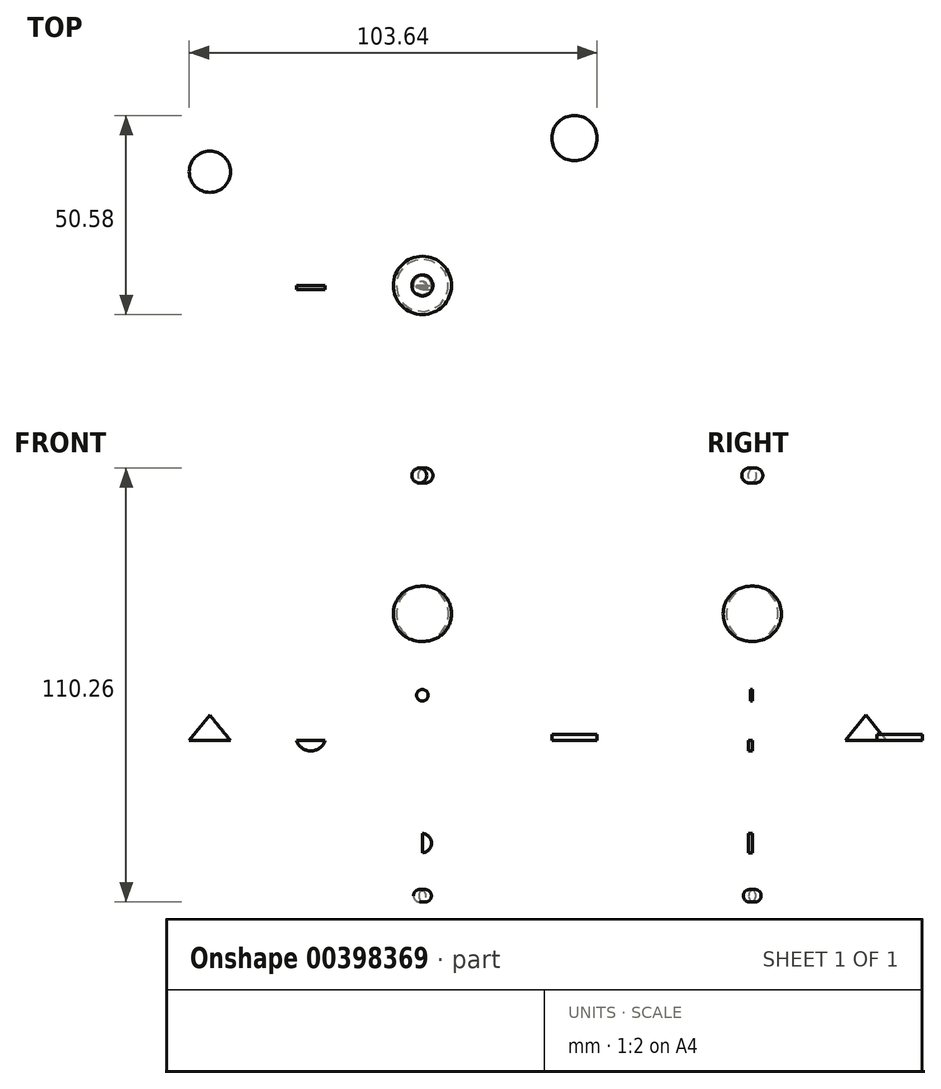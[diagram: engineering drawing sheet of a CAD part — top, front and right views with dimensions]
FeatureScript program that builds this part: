
annotation { "Feature Type Name" : "Feature", "Feature Type Description" : "" }
export const myFeature = defineFeature(function(context is Context, id is Id, definition is map)
    precondition{}
    {
        {
            var Q0;
            Q0=qCreatedBy(makeId("Front.planeOp"),FACE);
            var sketch = newSketch(context, id + "F0", { "sketchPlane" : qUnion([Q0])});
            skLineSegment(sketch, "E0", {"start": v(0, 39.22) * mm, "end": v(0, 25.22) * mm});
            skArc(sketch, "E1", {"start": v(0, 25.22) * mm, "mid": v(6.61, 32.22) * mm, "end": v(0, 39.22) * mm});
            skSolve(sketch);
        }
        {
            var Q0;
            Q0=makeQuery(id+"F0.imprint","IMPRINT",FACE,{"disambiguationData":[TD([[makeQuery(id+"F0.imprint","IMPRINT",EDGE,{"derivedFrom":sQuery(id+"F0.wireOp",EDGE,"E0")}),1.0]])]});
            var Q1;
            Q1=sQuery(id+"F0.wireOp",EDGE,"E0");
            revolve(context, id + "F1", {"entities" : qUnion([Q0]), "axis" : qUnion([Q1]), "revolveType" : RevolveType.FULL});
        }
        {
            var Q0;
            Q0=qCreatedBy(makeId("Top.planeOp"),FACE);
            var sketch = newSketch(context, id + "F2", { "sketchPlane" : qUnion([Q0])});
            skCircle(sketch, "E2", {"center": v(38.65, 37.42) * mm, "radius": 5.76 * mm});
            skPoint(sketch, "E2.first.point", {"position": v(40.8, 42.76) * mm});
            skPoint(sketch, "E2.second.point", {"position": v(33.3, 35.28) * mm});
            skPoint(sketch, "E2.third.point", {"position": v(34.88, 41.78) * mm});
            skSolve(sketch);
        }
        {
            var Q0;
            Q0=makeQuery(id+"F2.imprint","IMPRINT",FACE,{"disambiguationData":[TD([[makeQuery(id+"F2.imprint","IMPRINT",EDGE,{"derivedFrom":sQuery(id+"F2.wireOp",EDGE,"E2")}),1.0]])]});
            extrude(context, id + "F3", {"entities" : qUnion([Q0]), "depth" : 1.52 * mm});
        }
        {
            var Q0;
            Q0=qCreatedBy(makeId("Top.planeOp"),FACE);
            var sketch = newSketch(context, id + "F4", { "sketchPlane" : qUnion([Q0])});
            skCircle(sketch, "E3", {"center": v(-54, 28.87) * mm, "radius": 5.23 * mm});
            skPoint(sketch, "E3.first.point", {"position": v(-57.94, 25.42) * mm});
            skPoint(sketch, "E3.second.point", {"position": v(-50.45, 32.71) * mm});
            skPoint(sketch, "E3.third.point", {"position": v(-50.45, 25.03) * mm});
            skSolve(sketch);
        }
        {
            var Q0;
            Q0=makeQuery(id+"F4.imprint","IMPRINT",FACE,{"disambiguationData":[TD([[makeQuery(id+"F4.imprint","IMPRINT",EDGE,{"derivedFrom":sQuery(id+"F4.wireOp",EDGE,"E3")}),1.0]])]});
            extrude(context, id + "F5", {"entities" : qUnion([Q0]), "depth" : 7.62 * mm, "hasDraft" : true, "draftAngle" : 39 * degree, "draftPullDirection" : true});
        }
        {
            var Q0;
            Q0=qCreatedBy(makeId("Front.planeOp"),FACE);
            var sketch = newSketch(context, id + "F6", { "sketchPlane" : qUnion([Q0])});
            skLineSegment(sketch, "E4", {"start": v(0, -14.97) * mm, "end": v(0, -11.22) * mm});
            skArc(sketch, "E5", {"start": v(0, -14.97) * mm, "mid": v(2.44, -13.1) * mm, "end": v(0, -11.22) * mm});
            skSolve(sketch);
        }
        {
            var Q0;
            Q0=makeQuery(id+"F6.imprint","IMPRINT",FACE,{"disambiguationData":[TD([[makeQuery(id+"F6.imprint","IMPRINT",EDGE,{"derivedFrom":sQuery(id+"F6.wireOp",EDGE,"E4")}),-1.0]])]});
            var Q1;
            Q1=sQuery(id+"F6.wireOp",EDGE,"E4");
            revolve(context, id + "F7", {"entities" : qUnion([Q0]), "axis" : qUnion([Q1]), "revolveType" : RevolveType.FULL});
        }
        {
            var Q0;
            Q0=makeQuery(id+"F7.opRevolve","SWEPT_BODY",BODY,{"disambiguationData":[OSD([sQuery(id+"F6.wireOp",EDGE,"E4"),sQuery(id+"F6.wireOp",EDGE,"E5")])]});
            deleteBodies(context, id + "F8", {"entities" : qUnion([Q0])});
        }
        {
            var Q0;
            Q0=qCreatedBy(makeId("Front.planeOp"),FACE);
            var sketch = newSketch(context, id + "F9", { "sketchPlane" : qUnion([Q0])});
            skLineSegment(sketch, "E6", {"start": v(0, -40.87) * mm, "end": v(0, -38) * mm});
            skArc(sketch, "E7", {"start": v(0, -40.87) * mm, "mid": v(2.27, -39.43) * mm, "end": v(0, -38) * mm});
            skSolve(sketch);
        }
        {
            var Q0;
            Q0=makeQuery(id+"F9.imprint","IMPRINT",FACE,{"disambiguationData":[TD([[makeQuery(id+"F9.imprint","IMPRINT",EDGE,{"derivedFrom":sQuery(id+"F9.wireOp",EDGE,"E6")}),-1.0]])]});
            var Q1;
            Q1=sQuery(id+"F9.wireOp",EDGE,"E6");
            revolve(context, id + "F10", {"entities" : qUnion([Q0]), "axis" : qUnion([Q1]), "revolveType" : RevolveType.FULL});
        }
        {
            var Q0;
            Q0=qCreatedBy(makeId("Front.planeOp"),FACE);
            var sketch = newSketch(context, id + "F11", { "sketchPlane" : qUnion([Q0])});
            skLineSegment(sketch, "E8", {"start": v(0, -28.5) * mm, "end": v(0, -23.6) * mm});
            skArc(sketch, "E9", {"start": v(0, -28.5) * mm, "mid": v(2.3, -26.05) * mm, "end": v(0, -23.6) * mm});
            skSolve(sketch);
        }
        {
            var Q0;
            Q0=makeQuery(id+"F11.imprint","IMPRINT",FACE,{"disambiguationData":[TD([[makeQuery(id+"F11.imprint","IMPRINT",EDGE,{"derivedFrom":sQuery(id+"F11.wireOp",EDGE,"E8")}),-1.0]])]});
            extrude(context, id + "F12", {"entities" : qUnion([Q0]), "depth" : 1.02 * mm});
        }
        {
            var Q0;
            Q0=qCreatedBy(makeId("Front.planeOp"),FACE);
            var sketch = newSketch(context, id + "F13", { "sketchPlane" : qUnion([Q0])});
            skLineSegment(sketch, "E10", {"start": v(-31.95, 0) * mm, "end": v(-24.75, 0) * mm});
            skArc(sketch, "E11", {"start": v(-31.95, 0) * mm, "mid": v(-28.35, -2.63) * mm, "end": v(-24.75, 0) * mm});
            skSolve(sketch);
        }
        {
            var Q0;
            Q0=makeQuery(id+"F13.imprint","IMPRINT",FACE,{"disambiguationData":[TD([[makeQuery(id+"F13.imprint","IMPRINT",EDGE,{"derivedFrom":sQuery(id+"F13.wireOp",EDGE,"E10")}),-1.0]])]});
            extrude(context, id + "F14", {"entities" : qUnion([Q0]), "depth" : 1.02 * mm});
        }
        {
            var Q0;
            Q0=qCreatedBy(makeId("Front.planeOp"),FACE);
            var sketch = newSketch(context, id + "F15", { "sketchPlane" : qUnion([Q0])});
            skLineSegment(sketch, "E12", {"start": v(0, 69.07) * mm, "end": v(0, 65.62) * mm});
            skArc(sketch, "E13", {"start": v(0, 65.62) * mm, "mid": v(2.43, 67.35) * mm, "end": v(0, 69.07) * mm});
            skSolve(sketch);
        }
        {
            var Q0;
            Q0=makeQuery(id+"F15.imprint","IMPRINT",FACE,{"disambiguationData":[TD([[makeQuery(id+"F15.imprint","IMPRINT",EDGE,{"derivedFrom":sQuery(id+"F15.wireOp",EDGE,"E12")}),1.0]])]});
            var Q1;
            Q1=sQuery(id+"F15.wireOp",EDGE,"E12");
            revolve(context, id + "F16", {"entities" : qUnion([Q0]), "axis" : qUnion([Q1]), "revolveType" : RevolveType.TWO_DIRECTIONS, "angle" : 95 * degree, "angleBack" : 262.6 * degree});
        }
        {
            var Q0;
            Q0=makeQuery(id+"F16.opRevolve","SWEPT_BODY",BODY,{"disambiguationData":[OSD([sQuery(id+"F15.wireOp",EDGE,"E12"),sQuery(id+"F15.wireOp",EDGE,"E13")])]});
            deleteBodies(context, id + "F17", {"entities" : qUnion([Q0])});
        }
        {
            var Q0;
            Q0=qCreatedBy(makeId("Front.planeOp"),FACE);
            var sketch = newSketch(context, id + "F18", { "sketchPlane" : qUnion([Q0])});
            skLineSegment(sketch, "E14", {"start": v(0, 65.62) * mm, "end": v(0, 69.07) * mm});
            skArc(sketch, "E15", {"start": v(0, 65.62) * mm, "mid": v(2.68, 67.35) * mm, "end": v(0, 69.07) * mm});
            skSolve(sketch);
        }
        {
            var Q0;
            Q0=makeQuery(id+"F18.imprint","IMPRINT",FACE,{"disambiguationData":[TD([[makeQuery(id+"F18.imprint","IMPRINT",EDGE,{"derivedFrom":sQuery(id+"F18.wireOp",EDGE,"E14")}),-1.0]])]});
            var Q1;
            Q1=sQuery(id+"F18.wireOp",EDGE,"E14");
            revolve(context, id + "F19", {"entities" : qUnion([Q0]), "axis" : qUnion([Q1]), "revolveType" : RevolveType.FULL});
        }
        {
            var Q0;
            Q0=qCreatedBy(makeId("Front.planeOp"),FACE);
            var sketch = newSketch(context, id + "F20", { "sketchPlane" : qUnion([Q0])});
            skCircle(sketch, "E16", {"center": v(0, 11.51) * mm, "radius": 1.47 * mm});
            skSolve(sketch);
        }
        {
            var Q0;
            Q0=makeQuery(id+"F20.imprint","IMPRINT",FACE,{"disambiguationData":[TD([[makeQuery(id+"F20.imprint","IMPRINT",EDGE,{"derivedFrom":sQuery(id+"F20.wireOp",EDGE,"E16")}),1.0]])]});
            extrude(context, id + "F21", {"entities" : qUnion([Q0]), "depth" : 0.5 * mm});
        }
    });
